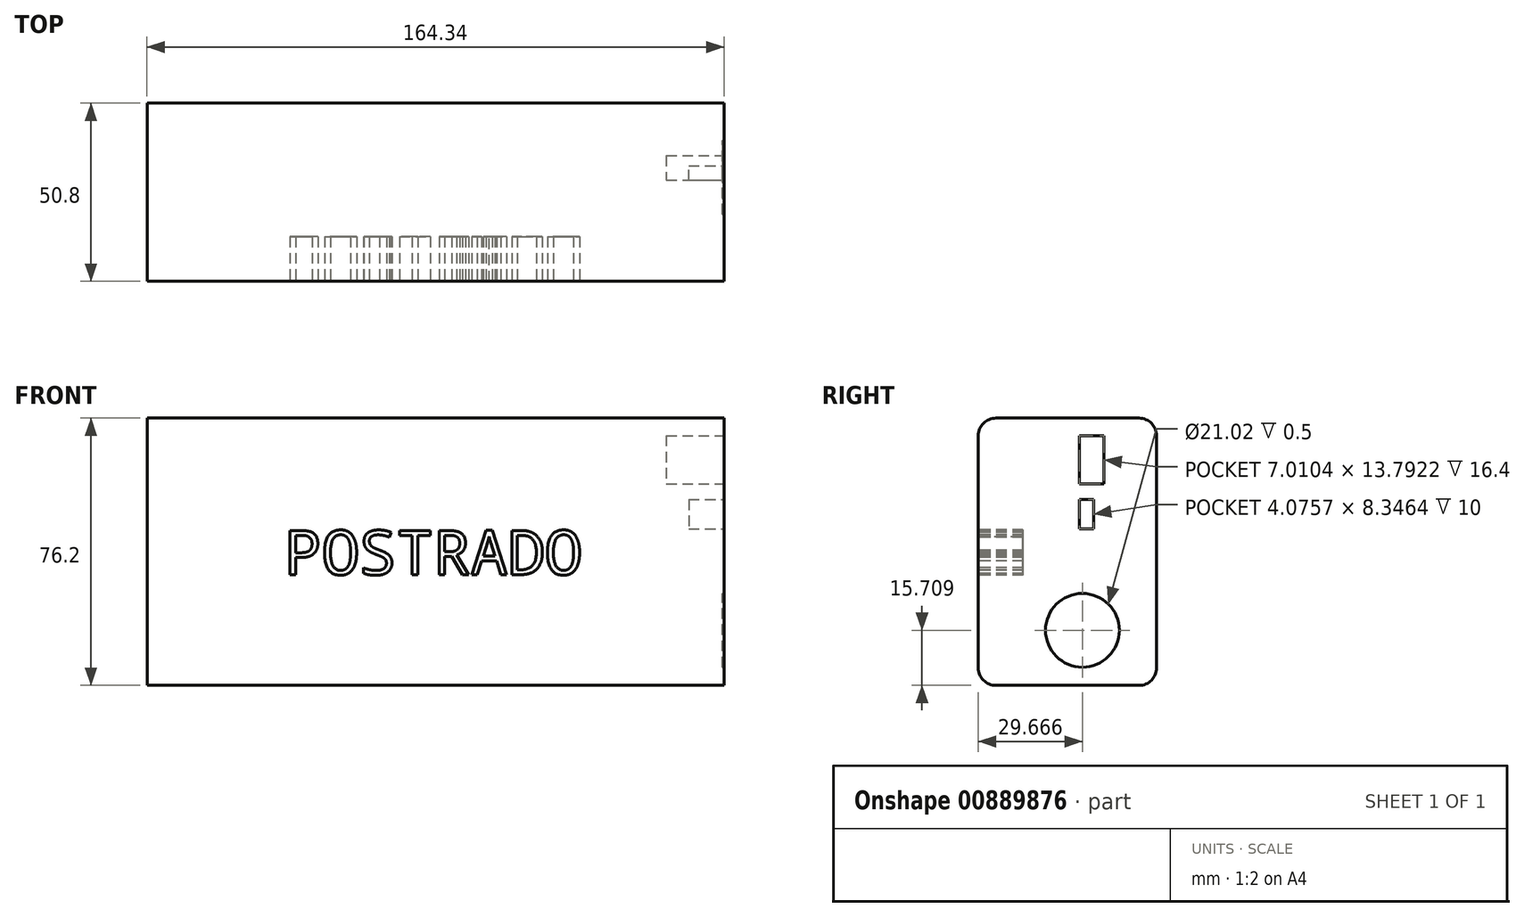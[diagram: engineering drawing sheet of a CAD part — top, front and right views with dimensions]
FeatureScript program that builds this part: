
annotation { "Feature Type Name" : "Feature", "Feature Type Description" : "" }
export const myFeature = defineFeature(function(context is Context, id is Id, definition is map)
    precondition{}
    {
        {
            var Q0;
            Q0=qCreatedBy(makeId("Front.planeOp"),FACE);
            var sketch = newSketch(context, id + "F0", { "sketchPlane" : qUnion([Q0])});
            skLineSegment(sketch, "E0.bottom", {"start": v(-82.17, 38.1) * mm, "end": v(82.17, 38.1) * mm});
            skLineSegment(sketch, "E0.top", {"start": v(-82.17, -38.1) * mm, "end": v(82.17, -38.1) * mm});
            skLineSegment(sketch, "E0.left", {"start": v(-82.17, 38.1) * mm, "end": v(-82.17, -38.1) * mm});
            skLineSegment(sketch, "E0.right", {"start": v(82.17, 38.1) * mm, "end": v(82.17, -38.1) * mm});
            skPoint(sketch, "E0.middle", {"position": v(0, 0) * mm});
            skSolve(sketch);
        }
        {
            var Q0;
            Q0=makeQuery(id+"F0.imprint","IMPRINT",FACE,{"disambiguationData":[TD([[makeQuery(id+"F0.imprint","IMPRINT",EDGE,{"derivedFrom":sQuery(id+"F0.wireOp",EDGE,"E0.bottom")}),-1.0]])]});
            extrude(context, id + "F1", {"entities" : qUnion([Q0]), "depth" : 50.8 * mm, "offsetDistance" : 25.4 * mm});
        }
        {
            var Q0;
            Q0=makeQuery(id+"F1.opExtrude","CAP_EDGE",EDGE,{"disambiguationData":[OSD([sQuery(id+"F0.wireOp",EDGE,"E0.bottom")])],"isStart":false});
            fillet(context, id + "F2", {"entities" : qUnion([Q0]), "radius" : 5 * mm, "tangentPropagation" : true, "allowEdgeOverflow" : false});
        }
        {
            var Q0;
            Q0=makeQuery(id+"F1.opExtrude","CAP_EDGE",EDGE,{"disambiguationData":[OSD([sQuery(id+"F0.wireOp",EDGE,"E0.bottom")])],"isStart":true});
            fillet(context, id + "F3", {"entities" : qUnion([Q0]), "radius" : 5 * mm, "tangentPropagation" : true, "allowEdgeOverflow" : false});
        }
        {
            var Q0;
            Q0=makeQuery(id+"F1.opExtrude","CAP_EDGE",EDGE,{"disambiguationData":[OSD([sQuery(id+"F0.wireOp",EDGE,"E0.top")])],"isStart":false});
            var Q1;
            Q1=makeQuery(id+"F1.opExtrude","CAP_EDGE",EDGE,{"disambiguationData":[OSD([sQuery(id+"F0.wireOp",EDGE,"E0.top")])],"isStart":true});
            fillet(context, id + "F4", {"entities" : qUnion([Q0, Q1]), "radius" : 5 * mm, "tangentPropagation" : true, "allowEdgeOverflow" : false});
        }
        {
            var Q0;
            Q0=makeQuery(id+"F1.opExtrude","SWEPT_FACE",FACE,{"disambiguationData":[OSD([sQuery(id+"F0.wireOp",EDGE,"E0.right")])]});
            var sketch = newSketch(context, id + "F5", { "sketchPlane" : qUnion([Q0])});
            skLineSegment(sketch, "E1.bottom", {"start": v(-14.97, 33.1) * mm, "end": v(-21.98, 33.1) * mm});
            skLineSegment(sketch, "E1.top", {"start": v(-14.97, 19.3) * mm, "end": v(-21.98, 19.3) * mm});
            skLineSegment(sketch, "E1.left", {"start": v(-14.97, 33.1) * mm, "end": v(-14.97, 19.3) * mm});
            skLineSegment(sketch, "E1.right", {"start": v(-21.98, 33.1) * mm, "end": v(-21.98, 19.3) * mm});
            skLineSegment(sketch, "E2.bottom", {"start": v(-21.98, 33.1) * mm, "end": v(-21.98, 33.1) * mm});
            skLineSegment(sketch, "E2.top", {"start": v(-21.98, 28.47) * mm, "end": v(-21.98, 28.47) * mm});
            skLineSegment(sketch, "E2.left", {"start": v(-21.98, 33.1) * mm, "end": v(-21.98, 28.47) * mm});
            skLineSegment(sketch, "E2.right", {"start": v(-21.98, 33.1) * mm, "end": v(-21.98, 28.47) * mm});
            skSolve(sketch);
        }
        {
            var Q0;
            Q0=makeQuery(id+"F5.imprint","IMPRINT",FACE,{"disambiguationData":[TD([[makeQuery(id+"F5.imprint","IMPRINT",EDGE,{"derivedFrom":sQuery(id+"F5.wireOp",EDGE,"E1.bottom")}),1.0]])]});
            extrude(context, id + "F6", {"entities" : qUnion([Q0]), "operationType" : NewBodyOperationType.REMOVE, "oppositeDirection" : true, "depth" : 16.4 * mm, "offsetDistance" : 25.4 * mm});
        }
        {
            var Q0;
            Q0=makeQuery(id+"F1.opExtrude","SWEPT_FACE",FACE,{"disambiguationData":[OSD([sQuery(id+"F0.wireOp",EDGE,"E0.right")])]});
            var sketch = newSketch(context, id + "F7", { "sketchPlane" : qUnion([Q0])});
            skLineSegment(sketch, "E3.bottom", {"start": v(-21.98, 14.9) * mm, "end": v(-17.9, 14.9) * mm});
            skLineSegment(sketch, "E3.top", {"start": v(-21.98, 6.56) * mm, "end": v(-17.9, 6.56) * mm});
            skLineSegment(sketch, "E3.left", {"start": v(-21.98, 14.9) * mm, "end": v(-21.98, 6.56) * mm});
            skLineSegment(sketch, "E3.right", {"start": v(-17.9, 14.9) * mm, "end": v(-17.9, 6.56) * mm});
            skSolve(sketch);
        }
        {
            var Q0;
            Q0 = qSketchRegion(id + "F7", true);
            extrude(context, id + "F8", {"entities" : qUnion([Q0]), "operationType" : NewBodyOperationType.REMOVE, "oppositeDirection" : true, "depth" : 10 * mm, "offsetDistance" : 25.4 * mm});
        }
        {
            var Q0;
            Q0=makeQuery(id+"F1.opExtrude","SWEPT_FACE",FACE,{"disambiguationData":[OSD([sQuery(id+"F0.wireOp",EDGE,"E0.right")])]});
            var sketch = newSketch(context, id + "F9", { "sketchPlane" : qUnion([Q0])});
            skCircle(sketch, "E4", {"center": v(-21.13, -22.4) * mm, "radius": 10.5 * mm});
            skPoint(sketch, "E4.first.point", {"position": v(-27.77, -14.25) * mm});
            skPoint(sketch, "E4.second.point", {"position": v(-13.67, -29.79) * mm});
            skPoint(sketch, "E4.third.point", {"position": v(-20, -11.94) * mm});
            skSolve(sketch);
        }
        {
            var Q0;
            Q0=makeQuery(id+"F9.imprint","IMPRINT",FACE,{"disambiguationData":[TD([[makeQuery(id+"F9.imprint","IMPRINT",EDGE,{"derivedFrom":sQuery(id+"F9.wireOp",EDGE,"E4")}),1.0]])]});
            extrude(context, id + "F10", {"entities" : qUnion([Q0]), "operationType" : NewBodyOperationType.REMOVE, "oppositeDirection" : true, "depth" : .5 * mm, "offsetDistance" : 25.4 * mm});
        }
        {
            var Q0;
            Q0=makeQuery(id+"F1.opExtrude","CAP_FACE",FACE,{"disambiguationData":[OSD([sQuery(id+"F0.wireOp",EDGE,"E0.bottom"),sQuery(id+"F0.wireOp",EDGE,"E0.top"),sQuery(id+"F0.wireOp",EDGE,"E0.left"),sQuery(id+"F0.wireOp",EDGE,"E0.right")])],"isStart":false});
            var sketch = newSketch(context, id + "F11", { "sketchPlane" : qUnion([Q0])});
            skText(sketch, "E5", { "text": "POSTRADO", "fontName": "DroidSansMono.ttf"});
            const initialGuessF11  = {"E5": [-0.04292, -0.00653, 1, 0, 0.0127]};
            skSetInitialGuess(sketch, initialGuessF11);
            skSolve(sketch);
        }
        {
            var Q0;
            Q0 = qSketchRegion(id + "F11", true);
            extrude(context, id + "F12", {"entities" : qUnion([Q0]), "operationType" : NewBodyOperationType.REMOVE, "oppositeDirection" : true, "depth" : 12.7 * mm, "offsetDistance" : 25.4 * mm});
        }
    });
